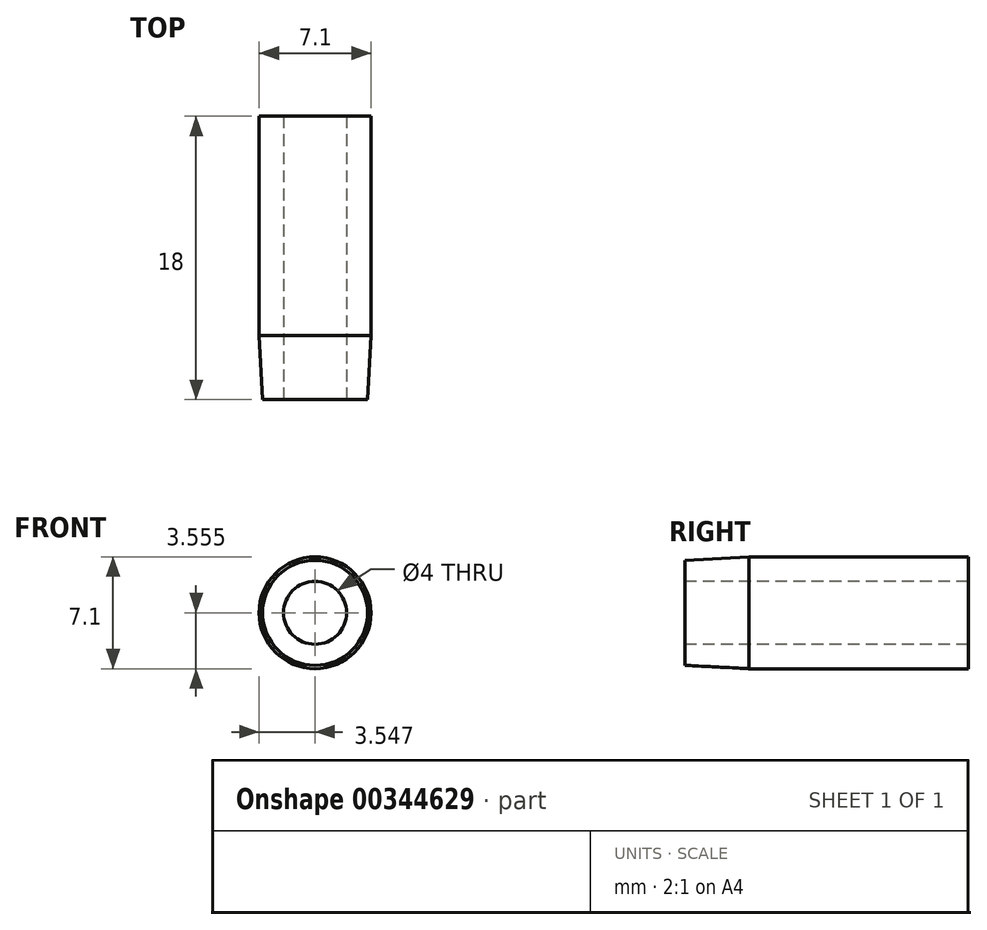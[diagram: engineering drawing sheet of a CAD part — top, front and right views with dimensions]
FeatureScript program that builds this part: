
annotation { "Feature Type Name" : "Feature", "Feature Type Description" : "" }
export const myFeature = defineFeature(function(context is Context, id is Id, definition is map)
    precondition{}
    {
        {
            var Q0;
            Q0=qCreatedBy(makeId("Front.planeOp"),FACE);
            var sketch = newSketch(context, id + "F0", { "sketchPlane" : qUnion([Q0])});
            skCircle(sketch, "E0", {"center": v(-36.08, 37.07) * mm, "radius": 3.55 * mm});
            skSolve(sketch);
        }
        {
            var Q0;
            Q0=qSketchRegion(id+"F0",true);
            extrude(context, id + "F1", {"entities" : qUnion([Q0]), "depth" : 25 * mm});
        }
        {
            var Q0;
            Q0=makeQuery(id+"F1.opExtrude","CAP_EDGE",EDGE,{"disambiguationData":[OSD([sQuery(id+"F0.wireOp",EDGE,"E0")])],"isStart":false});
            chamfer(context, id + "F2", {"entities" : qUnion([Q0]), "chamferType" : ChamferType.OFFSET_ANGLE, "width" : 1 * mm, "oppositeDirection" : false, "angle" : 87 * degree, "tangentPropagation" : true});
        }
        {
            var Q0;
            Q0=makeQuery(id+"F1.opExtrude","CAP_FACE",FACE,{"disambiguationData":[OSD([sQuery(id+"F0.wireOp",EDGE,"E0")])],"isStart":false});
            var sketch = newSketch(context, id + "F3", { "sketchPlane" : qUnion([Q0])});
            skCircle(sketch, "E1", {"center": v(-36.08, 37.07) * mm, "radius": 4.5 * mm});
            skSolve(sketch);
        }
        {
            var Q0;
            Q0=qSketchRegion(id+"F3",true);
            extrude(context, id + "F4", {"entities" : qUnion([Q0]), "operationType" : NewBodyOperationType.REMOVE, "oppositeDirection" : true, "depth" : 15 * mm});
        }
        {
            var Q0;
            Q0=makeQuery(id+"F4.boolean.opBoolean","COPY",FACE,{"derivedFrom":makeQuery(id+"F4.opExtrude","CAP_FACE",FACE,{"disambiguationData":[OSD([sQuery(id+"F3.wireOp",EDGE,"E1")])],"isStart":false})});
            var sketch = newSketch(context, id + "F5", { "sketchPlane" : qUnion([Q0])});
            skCircle(sketch, "E2", {"center": v(-36.08, 37.07) * mm, "radius": 2 * mm});
            skSolve(sketch);
        }
        {
            var Q0;
            Q0=qSketchRegion(id+"F5",true);
            extrude(context, id + "F6", {"entities" : qUnion([Q0]), "operationType" : NewBodyOperationType.REMOVE, "oppositeDirection" : true, "depth" : 25 * mm});
        }
        {
            var Q0;
            Q0=makeQuery(id+"F1.opExtrude","CAP_FACE",FACE,{"disambiguationData":[OSD([sQuery(id+"F0.wireOp",EDGE,"E0")])],"isStart":true});
            extrude(context, id + "F7", {"entities" : qUnion([Q0]), "operationType" : NewBodyOperationType.ADD, "depth" : 8 * mm});
        }
    });
